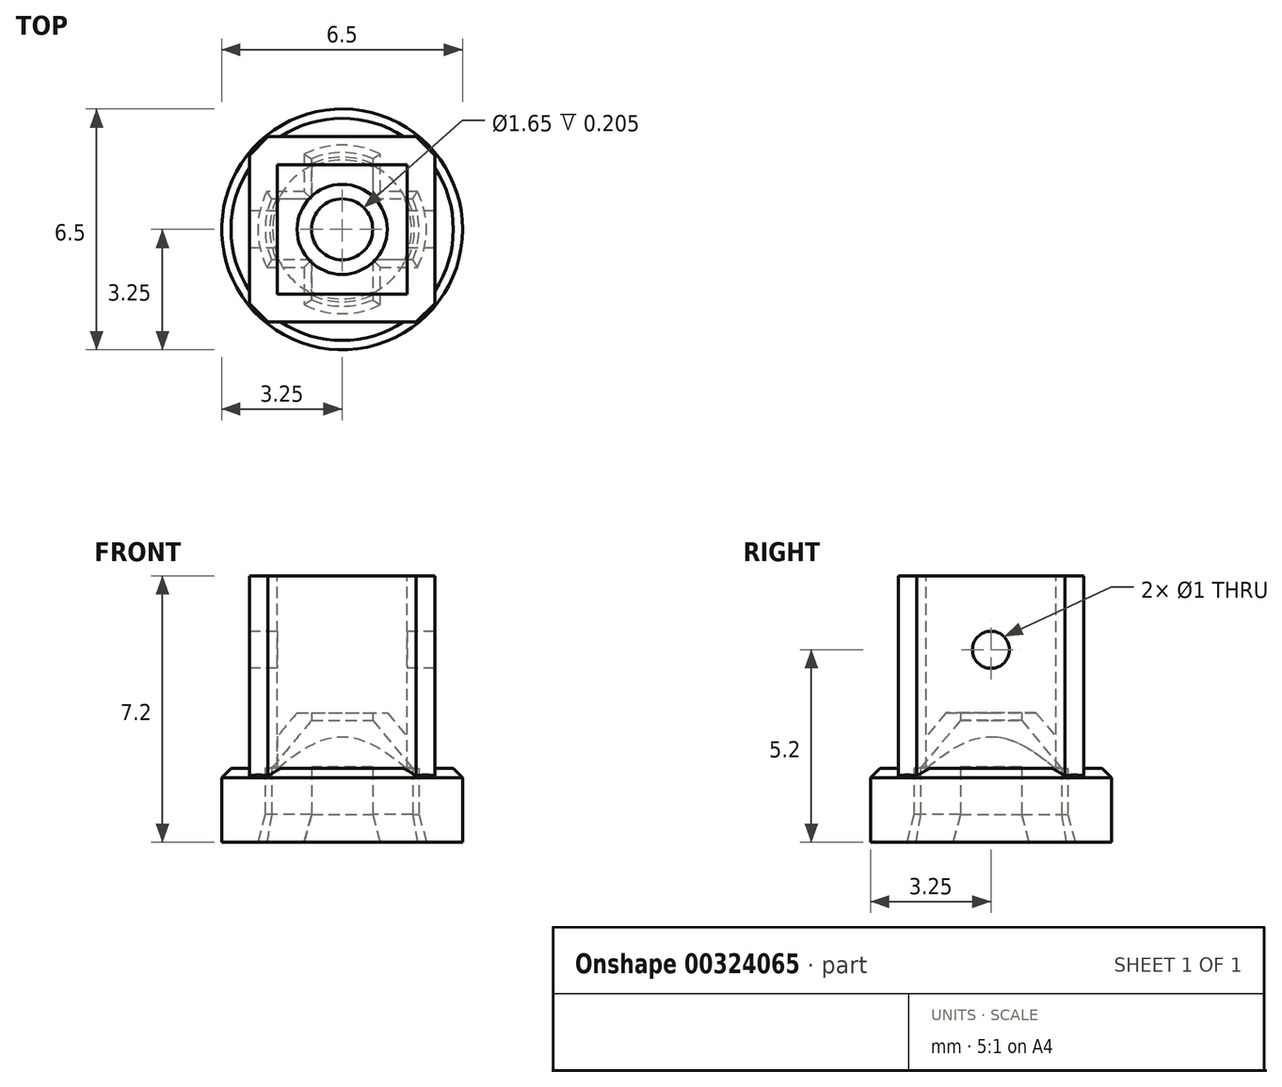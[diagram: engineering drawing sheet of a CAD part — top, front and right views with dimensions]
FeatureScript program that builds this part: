
annotation { "Feature Type Name" : "Feature", "Feature Type Description" : "" }
export const myFeature = defineFeature(function(context is Context, id is Id, definition is map)
    precondition{}
    {
        {
            var Q0;
            Q0=qCreatedBy(makeId("Top.planeOp"),FACE);
            var sketch = newSketch(context, id + "F0", { "sketchPlane" : qUnion([Q0])});
            skCircle(sketch, "E0", {"center": v(0, 0) * mm, "radius": 2.08 * mm});
            skLineSegment(sketch, "E1", {"start": v(-1.9, 0.82) * mm, "end": v(1.9, 0.82) * mm});
            skLineSegment(sketch, "E2", {"start": v(1.9, -0.82) * mm, "end": v(-1.9, -0.82) * mm});
            skLineSegment(sketch, "E3", {"start": v(-0.83, 1.9) * mm, "end": v(-0.83, -1.9) * mm});
            skLineSegment(sketch, "E4", {"start": v(0.82, 1.9) * mm, "end": v(0.82, -1.9) * mm});
            skCircle(sketch, "E5", {"center": v(0, 0) * mm, "radius": 3.25 * mm});
            skSolve(sketch);
        }
        {
            var Q0;
            Q0=makeQuery(id+"F0.imprint","IMPRINT",FACE,{"disambiguationData":[TD([[makeQuery(id+"F0.imprint","IMPRINT",EDGE,{"derivedFrom":sQuery(id+"F0.wireOp",EDGE,"E5")}),1.0]])]});
            var Q1;
            {var subQ0=sQuery(id+"F0.wireOp",EDGE,"E1");var subQ1=sQuery(id+"F0.wireOp",EDGE,"E0");var subQ2=makeQuery(id+"F0.imprint","INTERSECT",VERTEX,{"disambiguationData":[OD(1.0)],"derivedFrom":[subQ1,subQ0]});Q1=makeQuery(id+"F0.imprint","IMPRINT",FACE,{"disambiguationData":[TD([[makeQuery(id+"F0.imprint","IMPRINT",EDGE,{"disambiguationData":[TD([[subQ2,-1.0]])],"derivedFrom":subQ1}),1.0]])]});}
            var Q2;
            {var subQ0=sQuery(id+"F0.wireOp",EDGE,"E1");var subQ1=sQuery(id+"F0.wireOp",EDGE,"E0");var subQ2=makeQuery(id+"F0.imprint","INTERSECT",VERTEX,{"disambiguationData":[OD(0.0)],"derivedFrom":[subQ1,subQ0]});Q2=makeQuery(id+"F0.imprint","IMPRINT",FACE,{"disambiguationData":[TD([[makeQuery(id+"F0.imprint","IMPRINT",EDGE,{"disambiguationData":[TD([[subQ2,1.0]])],"derivedFrom":subQ1}),1.0]])]});}
            var Q3;
            {var subQ0=sQuery(id+"F0.wireOp",EDGE,"E2");var subQ1=sQuery(id+"F0.wireOp",EDGE,"E0");var subQ2=makeQuery(id+"F0.imprint","INTERSECT",VERTEX,{"disambiguationData":[OD(1.0)],"derivedFrom":[subQ1,subQ0]});Q3=makeQuery(id+"F0.imprint","IMPRINT",FACE,{"disambiguationData":[TD([[makeQuery(id+"F0.imprint","IMPRINT",EDGE,{"disambiguationData":[TD([[subQ2,-1.0]])],"derivedFrom":subQ1}),1.0]])]});}
            var Q4;
            {var subQ0=sQuery(id+"F0.wireOp",EDGE,"E2");var subQ1=sQuery(id+"F0.wireOp",EDGE,"E0");var subQ2=makeQuery(id+"F0.imprint","INTERSECT",VERTEX,{"disambiguationData":[OD(0.0)],"derivedFrom":[subQ1,subQ0]});Q4=makeQuery(id+"F0.imprint","IMPRINT",FACE,{"disambiguationData":[TD([[makeQuery(id+"F0.imprint","IMPRINT",EDGE,{"disambiguationData":[TD([[subQ2,1.0]])],"derivedFrom":subQ1}),1.0]])]});}
            extrude(context, id + "F1", {"entities" : qUnion([Q0, Q1, Q2, Q3, Q4]), "depth" : 2 * mm});
        }
        {
            var Q0;
            Q0=qCreatedBy(makeId("Front.planeOp"),FACE);
            var sketch = newSketch(context, id + "F2", { "sketchPlane" : qUnion([Q0])});
            skLineSegment(sketch, "E6.0", {"start": v(0.82, 2) * mm, "end": v(1.9, 2) * mm});
            skLineSegment(sketch, "E7.0", {"start": v(1.9, 2) * mm, "end": v(0.82, 2) * mm});
            skLineSegment(sketch, "E8.0", {"start": v(1.9, 2) * mm, "end": v(2.08, 2) * mm});
            skLineSegment(sketch, "E9", {"start": v(2.07, 2) * mm, "end": v(0.82, 3.5) * mm, "construction": true});
            skLineSegment(sketch, "E10", {"start": v(0.82, 3.5) * mm, "end": v(0.82, 2) * mm});
            skLineSegment(sketch, "E11", {"start": v(2.08, 2) * mm, "end": v(2.47, 2) * mm});
            skLineSegment(sketch, "E12", {"start": v(2.47, 2) * mm, "end": v(0.82, 3.97) * mm});
            skLineSegment(sketch, "E13", {"start": v(0.82, 3.97) * mm, "end": v(0.82, 3.5) * mm});
            skLineSegment(sketch, "E14", {"start": v(1.9, 2) * mm, "end": v(0.82, 3.3) * mm});
            skLineSegment(sketch, "E15", {"start": v(0.82, 3.5) * mm, "end": v(1.22, 3.5) * mm});
            skLineSegment(sketch, "E16", {"start": v(0, 0) * mm, "end": v(0, 3.97) * mm, "construction": true});
            skSolve(sketch);
        }
        {
            var Q0;
            Q0=makeQuery(id+"F2.imprint","IMPRINT",FACE,{"disambiguationData":[TD([[makeQuery(id+"F2.imprint","IMPRINT",EDGE,{"derivedFrom":sQuery(id+"F2.wireOp",EDGE,"E8.0")}),1.0]])]});
            var Q1;
            Q1=sQuery(id+"F2.wireOp",EDGE,"E16");
            var Q2;
            Q2=sQuery(id+"F2.wireOp",EDGE,"E16");
            revolve(context, id + "F3", {"operationType" : NewBodyOperationType.ADD, "entities" : qUnion([Q0]), "surfaceEntities" : qUnion([Q1]), "axis" : qUnion([Q2]), "revolveType" : RevolveType.FULL});
        }
        {
            var Q0;
            Q0=makeQuery(id+"F3.opRevolve","SWEPT_FACE",FACE,{"disambiguationData":[OSD([sQuery(id+"F2.wireOp",EDGE,"E15")])]});
            var sketch = newSketch(context, id + "F4", { "sketchPlane" : qUnion([Q0])});
            skLineSegment(sketch, "E17.bottom", {"start": v(2.5, 2.5) * mm, "end": v(-2.5, 2.5) * mm});
            skLineSegment(sketch, "E17.top", {"start": v(2.5, -2.5) * mm, "end": v(-2.5, -2.5) * mm});
            skLineSegment(sketch, "E17.left", {"start": v(2.5, 2.5) * mm, "end": v(2.5, -2.5) * mm});
            skLineSegment(sketch, "E17.right", {"start": v(-2.5, 2.5) * mm, "end": v(-2.5, -2.5) * mm});
            skPoint(sketch, "E17.middle", {"position": v(0, 0) * mm});
            skLineSegment(sketch, "E18.bottom", {"start": v(1.75, 1.75) * mm, "end": v(-1.75, 1.75) * mm});
            skLineSegment(sketch, "E18.top", {"start": v(1.75, -1.75) * mm, "end": v(-1.75, -1.75) * mm});
            skLineSegment(sketch, "E18.left", {"start": v(1.75, 1.75) * mm, "end": v(1.75, -1.75) * mm});
            skLineSegment(sketch, "E18.right", {"start": v(-1.75, 1.75) * mm, "end": v(-1.75, -1.75) * mm});
            skSolve(sketch);
        }
        {
            var Q0;
            Q0=makeQuery(id+"F4.imprint","IMPRINT",FACE,{"disambiguationData":[TD([[makeQuery(id+"F4.imprint","IMPRINT",EDGE,{"derivedFrom":sQuery(id+"F4.wireOp",EDGE,"E17.bottom")}),1.0]])]});
            var Q1;
            Q1=makeQuery(id+"F3.opRevolve","SWEPT_FACE",FACE,{"disambiguationData":[OSD([sQuery(id+"F2.wireOp",EDGE,"E12")])]});
            extrude(context, id + "F5", {"entities" : qUnion([Q0]), "operationType" : NewBodyOperationType.ADD, "endBound" : BoundingType.UP_TO_SURFACE, "oppositeDirection" : true, "endBoundEntityFace" : qUnion([Q1]), "depth" : 0.28 * mm});
        }
        {
            var Q0;
            Q0=makeQuery(id+"F5.opExtrude","CAP_FACE",FACE,{"disambiguationData":[OSD([sQuery(id+"F4.wireOp",EDGE,"E17.bottom"),sQuery(id+"F4.wireOp",EDGE,"E17.top"),sQuery(id+"F4.wireOp",EDGE,"E17.left"),sQuery(id+"F4.wireOp",EDGE,"E17.right"),sQuery(id+"F4.wireOp",EDGE,"E18.bottom"),sQuery(id+"F4.wireOp",EDGE,"E18.top"),sQuery(id+"F4.wireOp",EDGE,"E18.left"),sQuery(id+"F4.wireOp",EDGE,"E18.right")])],"isStart":true});
            extrude(context, id + "F6", {"entities" : qUnion([Q0]), "operationType" : NewBodyOperationType.ADD, "depth" : 3.7 * mm});
        }
        {
            var Q0;
            {var subQ0=sQuery(id+"F4.wireOp",EDGE,"E17.right");Q0=makeQuery(id+"F6.boolean.opBoolean","MERGE",FACE,{"derivedFrom":[makeQuery(id+"F5.opExtrude","SWEPT_FACE",FACE,{"disambiguationData":[OSD([subQ0])]}),makeQuery(id+"F6.opExtrude","SWEPT_FACE",FACE,{"disambiguationData":[OSD([subQ0])]})]});}
            var sketch = newSketch(context, id + "F7", { "sketchPlane" : qUnion([Q0])});
            skCircle(sketch, "E19", {"center": v(0, 5.2) * mm, "radius": 0.5 * mm});
            skPoint(sketch, "E19.centerSnap0", {"position": v(0, 7.2) * mm});
            skSolve(sketch);
        }
        {
            var Q0;
            Q0=makeQuery(id+"F7.imprint","IMPRINT",FACE,{"disambiguationData":[TD([[makeQuery(id+"F7.imprint","IMPRINT",EDGE,{"derivedFrom":sQuery(id+"F7.wireOp",EDGE,"E19")}),1.0]])]});
            extrude(context, id + "F8", {"entities" : qUnion([Q0]), "operationType" : NewBodyOperationType.REMOVE, "endBound" : BoundingType.THROUGH_ALL, "oppositeDirection" : true, "depth" : 25 * mm});
        }
        {
            var Q0;
            {var subQ0=sQuery(id+"F0.wireOp",EDGE,"E5");var subQ1=makeQuery(id+"F1.opExtrude","CAP_FACE",FACE,{"disambiguationData":[OSD([sQuery(id+"F0.wireOp",EDGE,"E0"),sQuery(id+"F0.wireOp",EDGE,"E1"),sQuery(id+"F0.wireOp",EDGE,"E2"),sQuery(id+"F0.wireOp",EDGE,"E3"),sQuery(id+"F0.wireOp",EDGE,"E4"),subQ0])],"isStart":false});var subQ2=makeQuery(id+"F1.opExtrude","SWEPT_FACE",FACE,{"disambiguationData":[OSD([subQ0])]});var subQ3=sQuery(id+"F4.wireOp",EDGE,"E17.top");Q0=makeQuery(id+"F5.boolean.opBoolean","SPLIT",EDGE,{"disambiguationData":[topologyDisambiguationEdgeConnected([subQ1,subQ2]),TD([makeQuery(id+"F5.opExtrude","SWEPT_FACE",FACE,{"disambiguationData":[OSD([subQ3])]})])],"derivedFrom":makeQuery(id+"F1.opExtrude","CAP_EDGE",EDGE,{"disambiguationData":[OSD([subQ0])],"isStart":false})});}
            var Q1;
            {var subQ0=sQuery(id+"F0.wireOp",EDGE,"E5");var subQ1=makeQuery(id+"F1.opExtrude","CAP_FACE",FACE,{"disambiguationData":[OSD([sQuery(id+"F0.wireOp",EDGE,"E0"),sQuery(id+"F0.wireOp",EDGE,"E1"),sQuery(id+"F0.wireOp",EDGE,"E2"),sQuery(id+"F0.wireOp",EDGE,"E3"),sQuery(id+"F0.wireOp",EDGE,"E4"),subQ0])],"isStart":false});var subQ2=sQuery(id+"F4.wireOp",EDGE,"E17.right");var subQ3=makeQuery(id+"F1.opExtrude","SWEPT_FACE",FACE,{"disambiguationData":[OSD([subQ0])]});Q1=makeQuery(id+"F5.boolean.opBoolean","SPLIT",EDGE,{"disambiguationData":[topologyDisambiguationEdgeConnected([subQ1,subQ3]),TD([makeQuery(id+"F5.opExtrude","SWEPT_FACE",FACE,{"disambiguationData":[OSD([subQ2])]})])],"derivedFrom":makeQuery(id+"F1.opExtrude","CAP_EDGE",EDGE,{"disambiguationData":[OSD([subQ0])],"isStart":false})});}
            var Q2;
            {var subQ0=sQuery(id+"F0.wireOp",EDGE,"E5");var subQ1=makeQuery(id+"F1.opExtrude","CAP_FACE",FACE,{"disambiguationData":[OSD([sQuery(id+"F0.wireOp",EDGE,"E0"),sQuery(id+"F0.wireOp",EDGE,"E1"),sQuery(id+"F0.wireOp",EDGE,"E2"),sQuery(id+"F0.wireOp",EDGE,"E3"),sQuery(id+"F0.wireOp",EDGE,"E4"),subQ0])],"isStart":false});var subQ2=sQuery(id+"F4.wireOp",EDGE,"E17.bottom");var subQ3=makeQuery(id+"F1.opExtrude","SWEPT_FACE",FACE,{"disambiguationData":[OSD([subQ0])]});Q2=makeQuery(id+"F5.boolean.opBoolean","SPLIT",EDGE,{"disambiguationData":[topologyDisambiguationEdgeConnected([subQ1,subQ3]),TD([makeQuery(id+"F5.opExtrude","SWEPT_FACE",FACE,{"disambiguationData":[OSD([subQ2])]})])],"derivedFrom":makeQuery(id+"F1.opExtrude","CAP_EDGE",EDGE,{"disambiguationData":[OSD([subQ0])],"isStart":false})});}
            var Q3;
            {var subQ0=sQuery(id+"F0.wireOp",EDGE,"E5");var subQ1=makeQuery(id+"F1.opExtrude","CAP_FACE",FACE,{"disambiguationData":[OSD([sQuery(id+"F0.wireOp",EDGE,"E0"),sQuery(id+"F0.wireOp",EDGE,"E1"),sQuery(id+"F0.wireOp",EDGE,"E2"),sQuery(id+"F0.wireOp",EDGE,"E3"),sQuery(id+"F0.wireOp",EDGE,"E4"),subQ0])],"isStart":false});var subQ2=makeQuery(id+"F1.opExtrude","SWEPT_FACE",FACE,{"disambiguationData":[OSD([subQ0])]});var subQ3=sQuery(id+"F4.wireOp",EDGE,"E17.left");Q3=makeQuery(id+"F5.boolean.opBoolean","SPLIT",EDGE,{"disambiguationData":[topologyDisambiguationEdgeConnected([subQ1,subQ2]),TD([makeQuery(id+"F5.opExtrude","SWEPT_FACE",FACE,{"disambiguationData":[OSD([subQ3])]})])],"derivedFrom":makeQuery(id+"F1.opExtrude","CAP_EDGE",EDGE,{"disambiguationData":[OSD([subQ0])],"isStart":false})});}
            chamfer(context, id + "F9", {"entities" : qUnion([Q0, Q1, Q2, Q3]), "width" : .25 * mm, "tangentPropagation" : true});
        }
        {
            var Q0;
            {var subQ0=sQuery(id+"F0.wireOp",EDGE,"E3");Q0=makeQuery(id+"F1.opExtrude","CAP_EDGE",EDGE,{"disambiguationData":[OSD([subQ0]),TDD([makeQuery(id+"F0.imprint","IMPRINT",EDGE,{"disambiguationData":[TD([[makeQuery(id+"F0.imprint","INTERSECT",VERTEX,{"disambiguationData":[OD(0.0)],"derivedFrom":[sQuery(id+"F0.wireOp",EDGE,"E0"),subQ0]}),-1.0]])],"derivedFrom":subQ0})])],"isStart":true});}
            var Q1;
            {var subQ0=sQuery(id+"F0.wireOp",EDGE,"E1");Q1=makeQuery(id+"F1.opExtrude","CAP_EDGE",EDGE,{"disambiguationData":[OSD([subQ0]),TDD([makeQuery(id+"F0.imprint","IMPRINT",EDGE,{"disambiguationData":[TD([[makeQuery(id+"F0.imprint","INTERSECT",VERTEX,{"disambiguationData":[OD(0.0)],"derivedFrom":[sQuery(id+"F0.wireOp",EDGE,"E0"),subQ0]}),-1.0]])],"derivedFrom":subQ0})])],"isStart":true});}
            var Q2;
            {var subQ0=sQuery(id+"F0.wireOp",EDGE,"E0");Q2=makeQuery(id+"F1.opExtrude","CAP_EDGE",EDGE,{"disambiguationData":[OSD([subQ0]),TDD([makeQuery(id+"F0.imprint","IMPRINT",EDGE,{"disambiguationData":[TD([[makeQuery(id+"F0.imprint","INTERSECT",VERTEX,{"disambiguationData":[OD(0.0)],"derivedFrom":[subQ0,sQuery(id+"F0.wireOp",EDGE,"E1")]}),-1.0]])],"derivedFrom":subQ0})])],"isStart":true});}
            var Q3;
            {var subQ0=sQuery(id+"F0.wireOp",EDGE,"E2");Q3=makeQuery(id+"F1.opExtrude","CAP_EDGE",EDGE,{"disambiguationData":[OSD([subQ0]),TDD([makeQuery(id+"F0.imprint","IMPRINT",EDGE,{"disambiguationData":[TD([[makeQuery(id+"F0.imprint","INTERSECT",VERTEX,{"disambiguationData":[OD(1.0)],"derivedFrom":[sQuery(id+"F0.wireOp",EDGE,"E0"),subQ0]}),1.0]])],"derivedFrom":subQ0})])],"isStart":true});}
            var Q4;
            {var subQ0=sQuery(id+"F0.wireOp",EDGE,"E3");Q4=makeQuery(id+"F1.opExtrude","CAP_EDGE",EDGE,{"disambiguationData":[OSD([subQ0]),TDD([makeQuery(id+"F0.imprint","IMPRINT",EDGE,{"disambiguationData":[TD([[makeQuery(id+"F0.imprint","INTERSECT",VERTEX,{"disambiguationData":[OD(1.0)],"derivedFrom":[sQuery(id+"F0.wireOp",EDGE,"E0"),subQ0]}),1.0]])],"derivedFrom":subQ0})])],"isStart":true});}
            var Q5;
            {var subQ0=sQuery(id+"F0.wireOp",EDGE,"E0");Q5=makeQuery(id+"F1.opExtrude","CAP_EDGE",EDGE,{"disambiguationData":[OSD([subQ0]),TDD([makeQuery(id+"F0.imprint","IMPRINT",EDGE,{"disambiguationData":[TD([[makeQuery(id+"F0.imprint","INTERSECT",VERTEX,{"disambiguationData":[OD(1.0)],"derivedFrom":[subQ0,sQuery(id+"F0.wireOp",EDGE,"E3")]}),-1.0]])],"derivedFrom":subQ0})])],"isStart":true});}
            var Q6;
            {var subQ0=sQuery(id+"F0.wireOp",EDGE,"E4");Q6=makeQuery(id+"F1.opExtrude","CAP_EDGE",EDGE,{"disambiguationData":[OSD([subQ0]),TDD([makeQuery(id+"F0.imprint","IMPRINT",EDGE,{"disambiguationData":[TD([[makeQuery(id+"F0.imprint","INTERSECT",VERTEX,{"disambiguationData":[OD(1.0)],"derivedFrom":[sQuery(id+"F0.wireOp",EDGE,"E0"),subQ0]}),1.0]])],"derivedFrom":subQ0})])],"isStart":true});}
            var Q7;
            {var subQ0=sQuery(id+"F0.wireOp",EDGE,"E2");Q7=makeQuery(id+"F1.opExtrude","CAP_EDGE",EDGE,{"disambiguationData":[OSD([subQ0]),TDD([makeQuery(id+"F0.imprint","IMPRINT",EDGE,{"disambiguationData":[TD([[makeQuery(id+"F0.imprint","INTERSECT",VERTEX,{"disambiguationData":[OD(0.0)],"derivedFrom":[sQuery(id+"F0.wireOp",EDGE,"E0"),subQ0]}),-1.0]])],"derivedFrom":subQ0})])],"isStart":true});}
            var Q8;
            {var subQ0=sQuery(id+"F0.wireOp",EDGE,"E0");Q8=makeQuery(id+"F1.opExtrude","CAP_EDGE",EDGE,{"disambiguationData":[OSD([subQ0]),TDD([makeQuery(id+"F0.imprint","IMPRINT",EDGE,{"disambiguationData":[TD([[makeQuery(id+"F0.imprint","INTERSECT",VERTEX,{"disambiguationData":[OD(1.0)],"derivedFrom":[subQ0,sQuery(id+"F0.wireOp",EDGE,"E1")]}),1.0]])],"derivedFrom":subQ0})])],"isStart":true});}
            var Q9;
            {var subQ0=sQuery(id+"F0.wireOp",EDGE,"E1");Q9=makeQuery(id+"F1.opExtrude","CAP_EDGE",EDGE,{"disambiguationData":[OSD([subQ0]),TDD([makeQuery(id+"F0.imprint","IMPRINT",EDGE,{"disambiguationData":[TD([[makeQuery(id+"F0.imprint","INTERSECT",VERTEX,{"disambiguationData":[OD(1.0)],"derivedFrom":[sQuery(id+"F0.wireOp",EDGE,"E0"),subQ0]}),1.0]])],"derivedFrom":subQ0})])],"isStart":true});}
            var Q10;
            {var subQ0=sQuery(id+"F0.wireOp",EDGE,"E4");Q10=makeQuery(id+"F1.opExtrude","CAP_EDGE",EDGE,{"disambiguationData":[OSD([subQ0]),TDD([makeQuery(id+"F0.imprint","IMPRINT",EDGE,{"disambiguationData":[TD([[makeQuery(id+"F0.imprint","INTERSECT",VERTEX,{"disambiguationData":[OD(0.0)],"derivedFrom":[sQuery(id+"F0.wireOp",EDGE,"E0"),subQ0]}),-1.0]])],"derivedFrom":subQ0})])],"isStart":true});}
            var Q11;
            {var subQ0=sQuery(id+"F0.wireOp",EDGE,"E0");Q11=makeQuery(id+"F1.opExtrude","CAP_EDGE",EDGE,{"disambiguationData":[OSD([subQ0]),TDD([makeQuery(id+"F0.imprint","IMPRINT",EDGE,{"disambiguationData":[TD([[makeQuery(id+"F0.imprint","INTERSECT",VERTEX,{"disambiguationData":[OD(0.0)],"derivedFrom":[subQ0,sQuery(id+"F0.wireOp",EDGE,"E3")]}),1.0]])],"derivedFrom":subQ0})])],"isStart":true});}
            chamfer(context, id + "F10", {"entities" : qUnion([Q0, Q1, Q2, Q3, Q4, Q5, Q6, Q7, Q8, Q9, Q10, Q11]), "chamferType" : ChamferType.TWO_OFFSETS, "width1" : .2 * mm, "oppositeDirection" : false, "width2" : .75 * mm, "tangentPropagation" : true});
        }
        {
            var Q0;
            {var subQ0=sQuery(id+"F2.wireOp",EDGE,"E8.0");var subQ1=makeQuery(id+"F3.opRevolve","SWEPT_FACE",FACE,{"disambiguationData":[OSD([subQ0,sQuery(id+"F2.wireOp",EDGE,"E11")])]});var subQ3=sQuery(id+"F0.wireOp",EDGE,"E0");var subQ5=sQuery(id+"F0.wireOp",EDGE,"E1");var subQ6=sQuery(id+"F2.wireOp",EDGE,"E14");var subQ7=makeQuery(id+"F3.opRevolve","SWEPT_FACE",FACE,{"disambiguationData":[OSD([subQ6])]});Q0=makeQuery(id+"F3.boolean.opBoolean","SPLIT",EDGE,{"disambiguationData":[topologyDisambiguationEdgeConnected([subQ1,subQ7]),TD([makeQuery(id+"F1.opExtrude","SWEPT_FACE",FACE,{"disambiguationData":[OSD([subQ5]),TDD([makeQuery(id+"F0.imprint","IMPRINT",EDGE,{"disambiguationData":[TD([[makeQuery(id+"F0.imprint","INTERSECT",VERTEX,{"disambiguationData":[OD(1.0)],"derivedFrom":[subQ3,subQ5]}),1.0]])],"derivedFrom":subQ5})])]})])],"derivedFrom":makeQuery(id+"F3.opRevolve","SWEPT_EDGE",EDGE,{"disambiguationData":[OSD([sQuery(id+"F2.wireOp",EDGE,"E7.0"),subQ0,subQ6])]})});}
            var Q1;
            {var subQ0=sQuery(id+"F2.wireOp",EDGE,"E8.0");var subQ1=makeQuery(id+"F3.opRevolve","SWEPT_FACE",FACE,{"disambiguationData":[OSD([subQ0,sQuery(id+"F2.wireOp",EDGE,"E11")])]});var subQ3=sQuery(id+"F0.wireOp",EDGE,"E0");var subQ5=sQuery(id+"F0.wireOp",EDGE,"E3");var subQ6=sQuery(id+"F2.wireOp",EDGE,"E14");var subQ7=makeQuery(id+"F3.opRevolve","SWEPT_FACE",FACE,{"disambiguationData":[OSD([subQ6])]});Q1=makeQuery(id+"F3.boolean.opBoolean","SPLIT",EDGE,{"disambiguationData":[topologyDisambiguationEdgeConnected([subQ1,subQ7]),TD([makeQuery(id+"F1.opExtrude","SWEPT_FACE",FACE,{"disambiguationData":[OSD([subQ5]),TDD([makeQuery(id+"F0.imprint","IMPRINT",EDGE,{"disambiguationData":[TD([[makeQuery(id+"F0.imprint","INTERSECT",VERTEX,{"disambiguationData":[OD(1.0)],"derivedFrom":[subQ3,subQ5]}),1.0]])],"derivedFrom":subQ5})])]})])],"derivedFrom":makeQuery(id+"F3.opRevolve","SWEPT_EDGE",EDGE,{"disambiguationData":[OSD([sQuery(id+"F2.wireOp",EDGE,"E7.0"),subQ0,subQ6])]})});}
            var Q2;
            {var subQ0=sQuery(id+"F2.wireOp",EDGE,"E8.0");var subQ1=makeQuery(id+"F3.opRevolve","SWEPT_FACE",FACE,{"disambiguationData":[OSD([subQ0,sQuery(id+"F2.wireOp",EDGE,"E11")])]});var subQ3=sQuery(id+"F0.wireOp",EDGE,"E0");var subQ5=sQuery(id+"F0.wireOp",EDGE,"E1");var subQ6=sQuery(id+"F2.wireOp",EDGE,"E14");var subQ7=makeQuery(id+"F3.opRevolve","SWEPT_FACE",FACE,{"disambiguationData":[OSD([subQ6])]});Q2=makeQuery(id+"F3.boolean.opBoolean","SPLIT",EDGE,{"disambiguationData":[topologyDisambiguationEdgeConnected([subQ1,subQ7]),TD([makeQuery(id+"F1.opExtrude","SWEPT_FACE",FACE,{"disambiguationData":[OSD([subQ5]),TDD([makeQuery(id+"F0.imprint","IMPRINT",EDGE,{"disambiguationData":[TD([[makeQuery(id+"F0.imprint","INTERSECT",VERTEX,{"disambiguationData":[OD(0.0)],"derivedFrom":[subQ3,subQ5]}),-1.0]])],"derivedFrom":subQ5})])]})])],"derivedFrom":makeQuery(id+"F3.opRevolve","SWEPT_EDGE",EDGE,{"disambiguationData":[OSD([sQuery(id+"F2.wireOp",EDGE,"E7.0"),subQ0,subQ6])]})});}
            var Q3;
            {var subQ0=sQuery(id+"F2.wireOp",EDGE,"E8.0");var subQ1=makeQuery(id+"F3.opRevolve","SWEPT_FACE",FACE,{"disambiguationData":[OSD([subQ0,sQuery(id+"F2.wireOp",EDGE,"E11")])]});var subQ3=sQuery(id+"F0.wireOp",EDGE,"E0");var subQ5=sQuery(id+"F0.wireOp",EDGE,"E3");var subQ6=sQuery(id+"F2.wireOp",EDGE,"E14");var subQ7=makeQuery(id+"F3.opRevolve","SWEPT_FACE",FACE,{"disambiguationData":[OSD([subQ6])]});Q3=makeQuery(id+"F3.boolean.opBoolean","SPLIT",EDGE,{"disambiguationData":[topologyDisambiguationEdgeConnected([subQ1,subQ7]),TD([makeQuery(id+"F1.opExtrude","SWEPT_FACE",FACE,{"disambiguationData":[OSD([subQ5]),TDD([makeQuery(id+"F0.imprint","IMPRINT",EDGE,{"disambiguationData":[TD([[makeQuery(id+"F0.imprint","INTERSECT",VERTEX,{"disambiguationData":[OD(0.0)],"derivedFrom":[subQ3,subQ5]}),-1.0]])],"derivedFrom":subQ5})])]})])],"derivedFrom":makeQuery(id+"F3.opRevolve","SWEPT_EDGE",EDGE,{"disambiguationData":[OSD([sQuery(id+"F2.wireOp",EDGE,"E7.0"),subQ0,subQ6])]})});}
            chamfer(context, id + "F11", {"entities" : qUnion([Q0, Q1, Q2, Q3]), "width" : .1 * mm, "tangentPropagation" : true});
        }
        {
            var Q0;
            {var subQ0=sQuery(id+"F4.wireOp",EDGE,"E17.left");var subQ1=sQuery(id+"F4.wireOp",EDGE,"E17.bottom");Q0=makeQuery(id+"F6.boolean.opBoolean","MERGE",EDGE,{"derivedFrom":[makeQuery(id+"F5.opExtrude","SWEPT_EDGE",EDGE,{"disambiguationData":[OSD([subQ1,subQ0])]}),makeQuery(id+"F6.opExtrude","SWEPT_EDGE",EDGE,{"disambiguationData":[OSD([subQ1,subQ0])]})]});}
            var Q1;
            {var subQ0=sQuery(id+"F4.wireOp",EDGE,"E17.left");var subQ1=sQuery(id+"F4.wireOp",EDGE,"E17.top");Q1=makeQuery(id+"F6.boolean.opBoolean","MERGE",EDGE,{"derivedFrom":[makeQuery(id+"F5.opExtrude","SWEPT_EDGE",EDGE,{"disambiguationData":[OSD([subQ1,subQ0])]}),makeQuery(id+"F6.opExtrude","SWEPT_EDGE",EDGE,{"disambiguationData":[OSD([subQ1,subQ0])]})]});}
            var Q2;
            {var subQ0=sQuery(id+"F4.wireOp",EDGE,"E17.right");var subQ1=sQuery(id+"F4.wireOp",EDGE,"E17.top");Q2=makeQuery(id+"F6.boolean.opBoolean","MERGE",EDGE,{"derivedFrom":[makeQuery(id+"F5.opExtrude","SWEPT_EDGE",EDGE,{"disambiguationData":[OSD([subQ1,subQ0])]}),makeQuery(id+"F6.opExtrude","SWEPT_EDGE",EDGE,{"disambiguationData":[OSD([subQ1,subQ0])]})]});}
            var Q3;
            {var subQ0=sQuery(id+"F4.wireOp",EDGE,"E17.right");var subQ1=sQuery(id+"F4.wireOp",EDGE,"E17.bottom");Q3=makeQuery(id+"F6.boolean.opBoolean","MERGE",EDGE,{"derivedFrom":[makeQuery(id+"F5.opExtrude","SWEPT_EDGE",EDGE,{"disambiguationData":[OSD([subQ1,subQ0])]}),makeQuery(id+"F6.opExtrude","SWEPT_EDGE",EDGE,{"disambiguationData":[OSD([subQ1,subQ0])]})]});}
            chamfer(context, id + "F12", {"entities" : qUnion([Q0, Q1, Q2, Q3]), "width" : .5 * mm, "tangentPropagation" : true});
        }
    });
